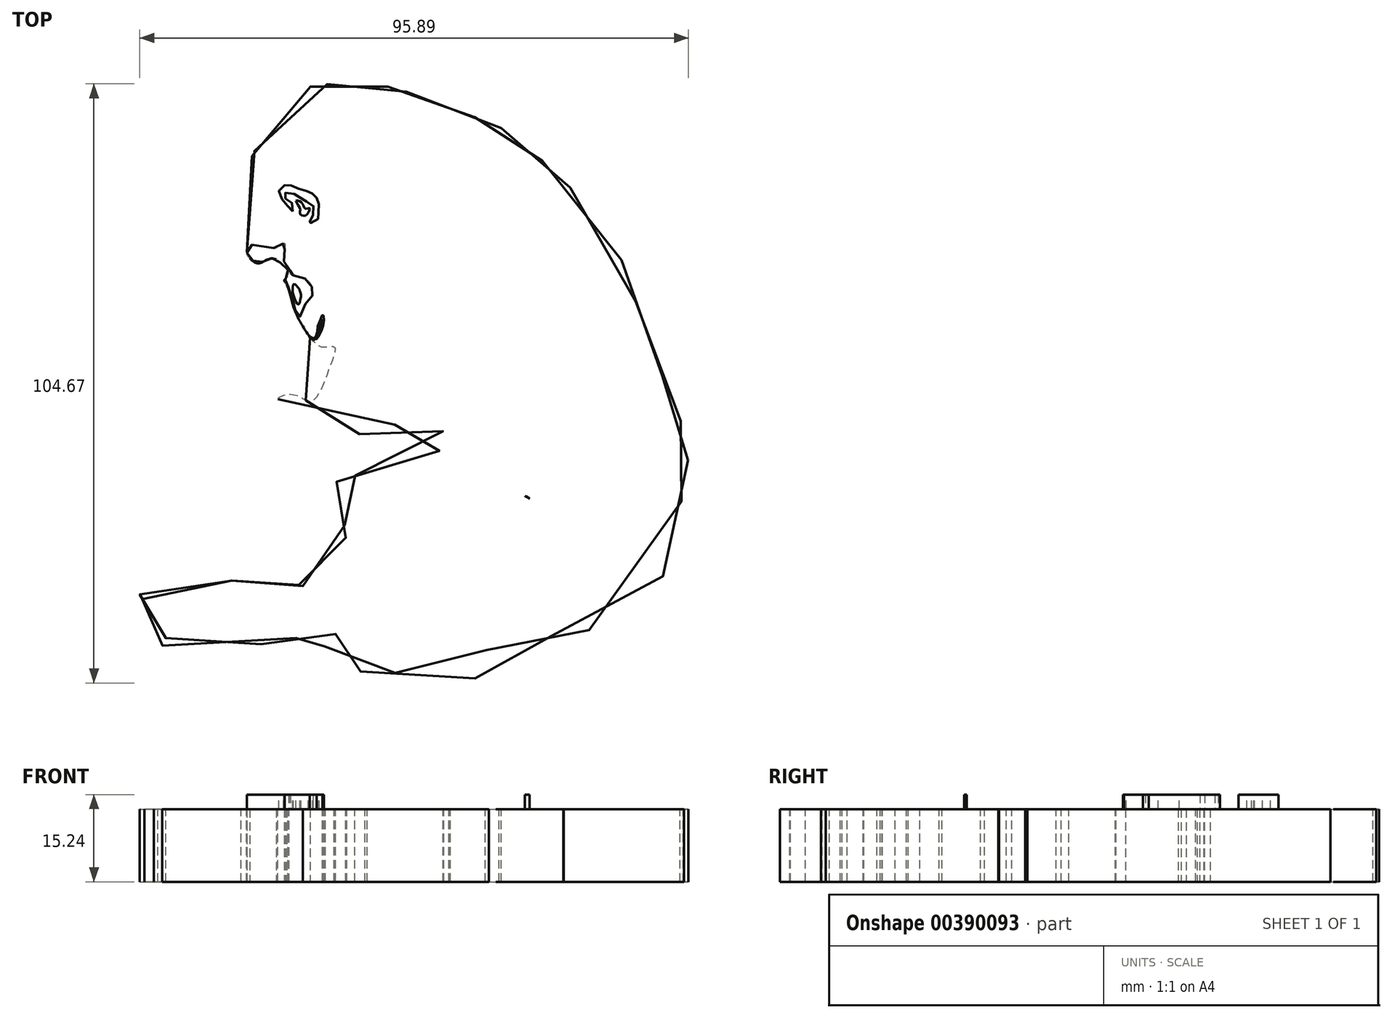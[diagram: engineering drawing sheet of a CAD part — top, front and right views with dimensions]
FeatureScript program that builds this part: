
annotation { "Feature Type Name" : "Feature", "Feature Type Description" : "" }
export const myFeature = defineFeature(function(context is Context, id is Id, definition is map)
    precondition{}
    {
        {
            var Q0;
            Q0=qCreatedBy(makeId("Top.planeOp"),FACE);
            var sketch = newSketch(context, id + "F0", { "sketchPlane" : qUnion([Q0])});
            skFitSpline(sketch, "E0", {"points": [v(-32.07, 25.4) * mm, v(-32.88, 29.05) * mm, v(-32.88, 31.33) * mm, v(-31.66, 35.38) * mm, v(-30.32, 38.34) * mm, v(-28.97, 40.5) * mm, v(-28.3, 42.65) * mm, v(-27.76, 44.54) * mm, v(-24.39, 47.77) * mm, v(-20.48, 49.11) * mm, v(-16.58, 49.25) * mm, v(-16.71, 48.58) * mm, v(-14.29, 48.85) * mm, v(-10.92, 49.38) * mm, v(-11.32, 48.58) * mm, v(-8.23, 48.98) * mm, v(-4.45, 48.3) * mm, v(0, 46.83) * mm, v(3.63, 46.02) * mm, v(3.36, 45.48) * mm, v(7.13, 44.4) * mm, v(7.53, 43.86) * mm, v(12.25, 42.11) * mm, v(12.38, 41.44) * mm, v(12.11, 41.03) * mm, v(13.73, 41.03) * mm, v(14.54, 40.36) * mm, v(16.42, 38.88) * mm, v(19.39, 36.32) * mm, v(22.62, 32.95) * mm, v(27.33, 29.05) * mm, v(29.49, 25.95) * mm, v(33.26, 19.62) * mm, v(34.34, 14.9) * mm, v(36.5, 10.46) * mm, v(38.24, 4.26) * mm, v(40.13, 0) * mm, v(41.48, -3.69) * mm, v(43.36, -7.73) * mm, v(44.3, -11.5) * mm, v(44.3, -12.3) * mm, v(43.77, -11.9) * mm, v(44.58, -14.46) * mm, v(45.11, -17.02) * mm, v(44.44, -16.89) * mm, v(44.44, -19.18) * mm, v(43.48, -26.54) * mm, v(42.15, -33.97) * mm, v(35.65, -42.08) * mm, v(28.4, -45.7) * mm, v(23.41, -47.06) * mm, v(23.41, -46.6) * mm, v(20.24, -47.29) * mm, v(15.03, -47.97) * mm, v(9.82, -48.2) * mm, v(10.27, -50.23) * mm, v(9.82, -52.72) * mm, v(7.56, -54.54) * mm, v(2.12, -54.99) * mm, v(-1.96, -53.63) * mm, v(-6.72, -53.4) * mm, v(-10.57, -53.4) * mm, v(-15.32, -52.5) * mm, v(-20.76, -51.36) * mm, v(-22.12, -50.23) * mm, v(-18.27, -48.65) * mm, v(-18.5, -47.74) * mm, v(-14.87, -46.15) * mm, v(-13.06, -45.02) * mm, v(-13.96, -43.44) * mm, v(-15.32, -44.34) * mm, v(-23.25, -47.29) * mm, v(-32.54, -49.33) * mm, v(-34.8, -50.68) * mm, v(-42.28, -49.78) * mm, v(-46.36, -49.33) * mm, v(-46.59, -47.97) * mm, v(-46.13, -47.06) * mm, v(-48.17, -45.7) * mm, v(-47.5, -44.34) * mm, v(-49.08, -44.57) * mm, v(-49.53, -41.85) * mm, v(-48.17, -40.5) * mm, v(-50.2, -40.5) * mm, v(-49.98, -37.77) * mm, v(-44.77, -35.73) * mm, v(-41.15, -35.05) * mm, v(-39.34, -36.19) * mm, v(-36.4, -37.32) * mm, v(-33, -37.32) * mm, v(-30.95, -37.32) * mm, v(-26.88, -30.75) * mm, v(-25.74, -33.47) * mm, v(-23.48, -37.55) * mm, v(-21.9, -38.23) * mm, v(-19.63, -36.87) * mm, v(-18.27, -34.6) * mm, v(-16.68, -32.79) * mm, v(-14.64, -33.02) * mm, v(-14.64, -31.66) * mm, v(-14.64, -29.62) * mm, v(-15.32, -26.9) * mm, v(-17.14, -27.35) * mm, v(-18.72, -25.09) * mm, v(-18.27, -21.46) * mm, v(-18.27, -19.42) * mm, v(-15.78, -20.1) * mm, v(-11.7, -18.06) * mm, v(-6.26, -15.8) * mm, v(-3.77, -14.67) * mm, v(0, -15.57) * mm, v(2.35, -13.53) * mm, v(2.35, -11.5) * mm, v(2.12, -8.32) * mm, v(0, -7.2) * mm, v(-3.1, -7.2) * mm, v(-5.36, -9.46) * mm, v(-9.43, -11.27) * mm, v(-13.96, -11.95) * mm, v(-17.82, -11.95) * mm, v(-25.83, -6.06) * mm, v(-26.5, -5.38) * mm, v(-24.01, -4.7) * mm, v(-21.52, -5.83) * mm, v(-20.39, -5.83) * mm, v(-18.58, -3.11) * mm, v(-17.44, 0) * mm, v(-16.54, 3.46) * mm, v(-18.58, 3.46) * mm, v(-20.39, 4.59) * mm, v(-21.98, 6.85) * mm, v(-23.79, 10.48) * mm, v(-24.92, 14.33) * mm, v(-25.37, 15.24) * mm, v(-24.47, 16.6) * mm, v(-26.28, 18.63) * mm, v(-28.32, 18.86) * mm, v(-29.68, 18.18) * mm, v(-31.04, 18.63) * mm, v(-31.94, 20) * mm, v(-31.94, 21.52) * mm, v(-32.07, 25.4) * mm]});
            skSolve(sketch);
        }
        {
            var Q0;
            Q0=makeQuery(id+"F0.imprint","IMPRINT",FACE,{"disambiguationData":[TD([[makeQuery(id+"F0.imprint","IMPRINT",EDGE,{"derivedFrom":sQuery(id+"F0.wireOp",EDGE,"E0")}),-1.0]])]});
            var sketch = newSketch(context, id + "F1", { "sketchPlane" : qUnion([Q0])});
            skFitSpline(sketch, "E1", {"points": [v(-31.96, 20.02) * mm, v(-31.24, 21.3) * mm, v(-30.43, 21.38) * mm, v(-28.03, 20.9) * mm, v(-26.35, 21.06) * mm, v(-25.39, 21.7) * mm, v(-25.39, 20.42) * mm, v(-25.39, 18.26) * mm, v(-24.35, 16.82) * mm, v(-24.35, 16.26) * mm, v(-22.75, 15.86) * mm, v(-20.98, 14.82) * mm, v(-20.42, 13.3) * mm, v(-20.58, 12.33) * mm, v(-21.95, 10.73) * mm, v(-22.83, 8.73) * mm, v(-23.63, 10.33) * mm, v(-23.95, 11.85) * mm, v(-24.9, 14.34) * mm, v(-25.3, 14.98) * mm, v(-24.67, 16.58) * mm, v(-25.55, 17.78) * mm, v(-26.75, 18.82) * mm, v(-28.11, 18.98) * mm, v(-29.55, 18.26) * mm, v(-31.08, 18.74) * mm, v(-31.96, 20.02) * mm]});
            skPoint(sketch, "E2.2.internal.orphan", {"position": v(-22.67, 13.3) * mm});
            skFitSpline(sketch, "E3", {"points": [v(-23.7, 14.6) * mm, v(-23.2, 14.18) * mm, v(-22.88, 13.75) * mm, v(-22.67, 13.3) * mm, v(-22.47, 12.68) * mm, v(-22.67, 11.6) * mm, v(-22.9, 10.96) * mm, v(-23.35, 11.42) * mm, v(-23.64, 12.13) * mm, v(-23.95, 13.3) * mm, v(-23.7, 14.6) * mm]});
            skFitSpline(sketch, "E4", {"points": [v(-20.93, 5.31) * mm, v(-20.42, 5.11) * mm, v(-20.12, 5) * mm, v(-19.76, 5.63) * mm, v(-19.6, 6.4) * mm, v(-19.53, 7.4) * mm, v(-19, 8.45) * mm, v(-18.65, 9.29) * mm, v(-18.52, 9) * mm, v(-18.48, 8.3) * mm, v(-18.59, 7.44) * mm, v(-18.94, 6.4) * mm, v(-19.55, 5.2) * mm, v(-19.76, 4.88) * mm, v(-19.38, 6.07) * mm, v(-19.1, 6.73) * mm, v(-18.8, 7.52) * mm, v(-18.74, 7.97) * mm, v(-18.84, 8.26) * mm, v(-19, 8.04) * mm, v(-19.26, 7.49) * mm, v(-19.4, 7.03) * mm, v(-19.43, 6.48) * mm, v(-19.5, 6.12) * mm, v(-19.66, 5.58) * mm, v(-19.95, 4.84) * mm, v(-20.42, 4.83) * mm, v(-20.93, 5.31) * mm]});
            skFitSpline(sketch, "E5", {"points": [v(-23.95, 27.26) * mm, v(-24.45, 27.83) * mm, v(-25.39, 28.68) * mm, v(-26.03, 29.81) * mm, v(-26.31, 31) * mm, v(-25.39, 31.8) * mm, v(-24.45, 31.9) * mm, v(-23.95, 31.57) * mm, v(-22.67, 31.11) * mm, v(-21.67, 30.89) * mm, v(-21.16, 30.6) * mm, v(-20.42, 30.32) * mm, v(-19.97, 29.81) * mm, v(-19.57, 29.47) * mm, v(-19.4, 28.62) * mm, v(-19.35, 27.43) * mm, v(-19.57, 26.53) * mm, v(-19.52, 25.9) * mm, v(-20.42, 25.45) * mm, v(-21.22, 24.94) * mm, v(-20.93, 25.4) * mm, v(-20.42, 26.3) * mm, v(-20.42, 27.54) * mm, v(-20.42, 28.56) * mm, v(-22.12, 29.13) * mm, v(-22.67, 29.64) * mm, v(-23.43, 30.04) * mm, v(-23.95, 30.43) * mm, v(-25.39, 30.38) * mm, v(-25.39, 29.7) * mm, v(-24.73, 29.19) * mm, v(-23.95, 28.45) * mm, v(-23.95, 27.26) * mm]});
            skFitSpline(sketch, "E6", {"points": [v(-23.37, 29.07) * mm, v(-22.67, 29.02) * mm, v(-22.12, 28.4) * mm, v(-21.67, 27.66) * mm, v(-21, 27.77) * mm, v(-21.39, 26.75) * mm, v(-22.12, 26.47) * mm, v(-22.67, 26.8) * mm, v(-22.67, 27.15) * mm, v(-22.67, 27.77) * mm, v(-23.37, 29.07) * mm]});
            skFitSpline(sketch, "E7", {"points": [v(-13.42, -43.37) * mm, v(-10.7, -42.4) * mm, v(-8.3, -41.29) * mm, v(-6.37, -40.49) * mm, v(-1.56, -38.56) * mm, v(7.57, -35.84) * mm, v(11.41, -33.12) * mm, v(12.7, -27.67) * mm, v(12.7, -21.42) * mm, v(11.9, -19.66) * mm, v(12.53, -19.02) * mm, v(12.7, -14.86) * mm, v(12.05, -9.09) * mm, v(10.93, -4.28) * mm, v(12.05, -4.28) * mm, v(12.21, -2.52) * mm, v(11.57, 2.12) * mm, v(8.69, 10.45) * mm], "startDerivative": vector(54.54, 17.43) * mm, "endDerivative": vector(-39.6, 100.35) * mm});
            skFitSpline(sketch, "E8", {"points": [v(-16.7, 3.9) * mm, v(-14.55, 4.36) * mm, v(-13.08, 5.04) * mm, v(-12.74, 7.65) * mm, v(-12.51, 9) * mm, v(-13.87, 7.99) * mm, v(-13.76, 9) * mm, v(-13.98, 15.12) * mm, v(-12.96, 19.77) * mm, v(-10.93, 23.05) * mm, v(-8.89, 24.94) * mm, v(-7.53, 27.43) * mm, v(-5.04, 28.62) * mm], "startDerivative": vector(28.51, 6.06) * mm, "endDerivative": vector(33.45, 9.35) * mm});
            skFitSpline(sketch, "E9", {"points": [v(12.82, -17.43) * mm, v(13.33, -19.02) * mm, v(14.57, -20.85) * mm, v(16.76, -22.57) * mm, v(20.95, -24.38) * mm, v(24.66, -25.33) * mm], "startDerivative": vector(2.55, -10.41) * mm, "endDerivative": vector(15.7, -3.44) * mm});
            skFitSpline(sketch, "E10", {"points": [v(16.47, -22.47) * mm, v(17.45, -22.94) * mm, v(17.9, -25.52) * mm, v(18.57, -27.43) * mm], "startDerivative": vector(4.45, -0.8) * mm, "endDerivative": vector(2.32, -4.85) * mm});
            skFitSpline(sketch, "E11", {"points": [v(-43.56, -35.71) * mm, v(-44.84, -36.43) * mm, v(-46.12, -37.95) * mm, v(-46.28, -38.6) * mm, v(-44.84, -38.27) * mm, v(-44.52, -38.2) * mm, v(-46.36, -40.04) * mm, v(-44.92, -39.72) * mm, v(-44.28, -39.64) * mm, v(-44.28, -40.44) * mm, v(-45.48, -41.08) * mm, v(-43.56, -42.2) * mm, v(-44.36, -42.68) * mm, v(-42.6, -42.84) * mm, v(-40.43, -43.96) * mm, v(-42.03, -44.04) * mm, v(-41.07, -44.6) * mm, v(-39.4, -45.32) * mm, v(-36.9, -46.12) * mm, v(-35.79, -47.08) * mm, v(-34.67, -47.16) * mm, v(-30.42, -48.53) * mm, v(-29.14, -48.77) * mm], "startDerivative": vector(-28.78, -12.63) * mm, "endDerivative": vector(24, -1.95) * mm});
            skSolve(sketch);
        }
        {
            var Q0;
            Q0 = qSketchRegion(id + "F0", true);
            extrude(context, id + "F2", {"entities" : qUnion([Q0]), "depth" : 12.7 * mm});
        }
        {
            var Q0;
            Q0 = qSketchRegion(id + "F1", true);
            extrude(context, id + "F3", {"entities" : qUnion([Q0]), "operationType" : NewBodyOperationType.ADD, "depth" : 15.24 * mm});
        }
    });
